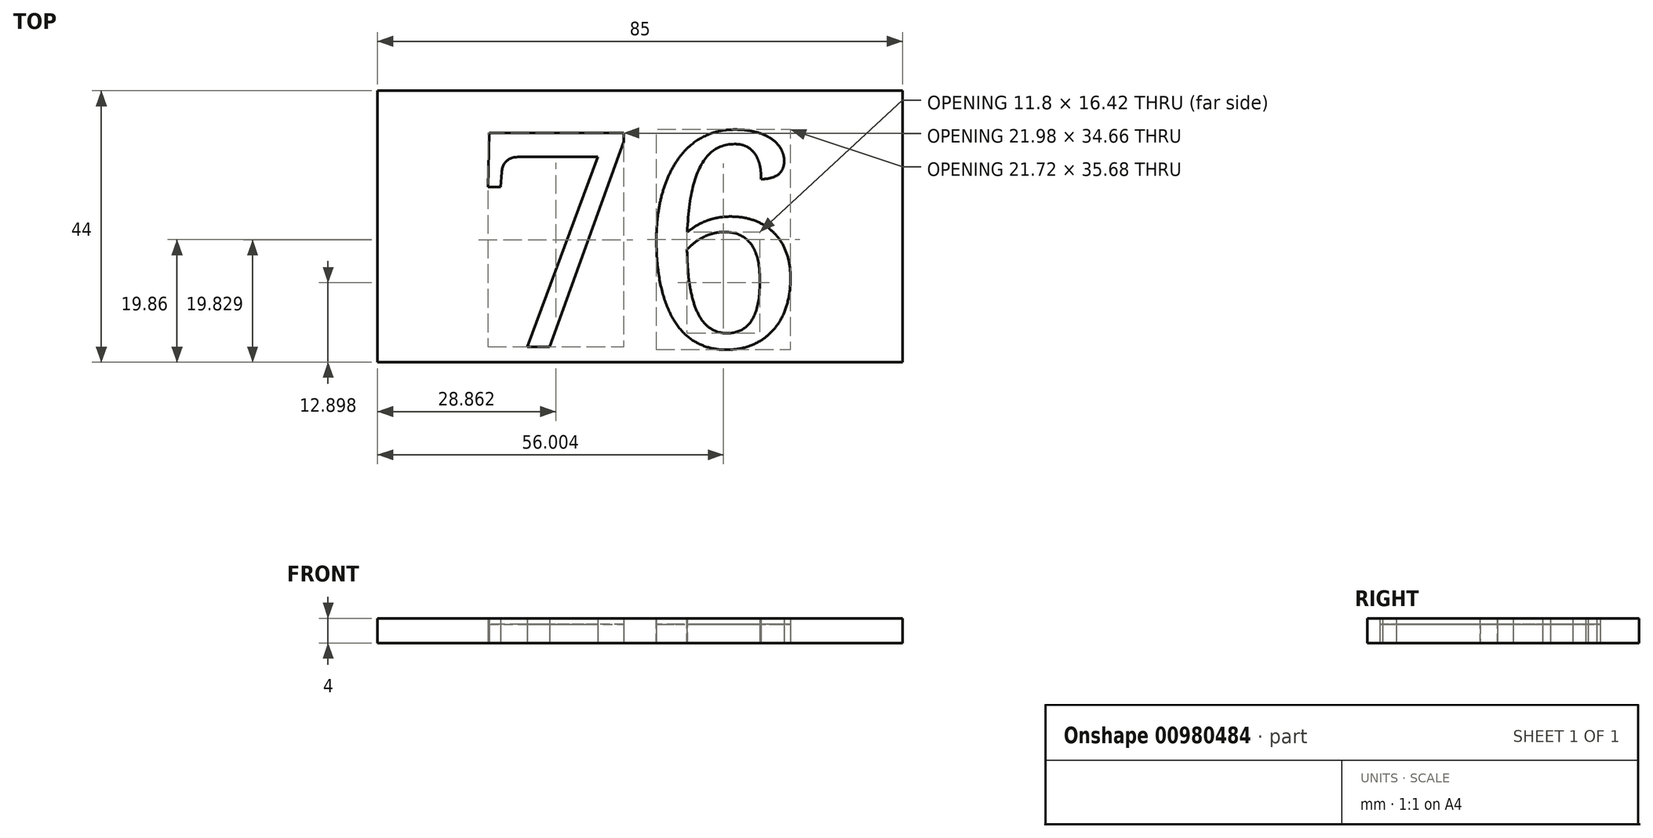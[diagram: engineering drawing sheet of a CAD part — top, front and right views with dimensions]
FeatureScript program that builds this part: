
annotation { "Feature Type Name" : "Feature", "Feature Type Description" : "" }
export const myFeature = defineFeature(function(context is Context, id is Id, definition is map)
    precondition{}
    {
        {
            var Q0;
            Q0=qCreatedBy(makeId("Top.planeOp"),FACE);
            var sketch = newSketch(context, id + "F0", { "sketchPlane" : qUnion([Q0])});
            skLineSegment(sketch, "E0.bottom", {"start": v(-42.5, 22) * mm, "end": v(42.5, 22) * mm});
            skLineSegment(sketch, "E0.top", {"start": v(-42.5, -22) * mm, "end": v(42.5, -22) * mm});
            skLineSegment(sketch, "E0.left", {"start": v(-42.5, 22) * mm, "end": v(-42.5, -22) * mm});
            skLineSegment(sketch, "E0.right", {"start": v(42.5, 22) * mm, "end": v(42.5, -22) * mm});
            skPoint(sketch, "E0.middle", {"position": v(0, 0) * mm});
            skText(sketch, "E1", { "text": "76\n", "fontName": "NotoSerif-Regular.ttf"});
            const initialGuessF0  = {"E1": [-0.0275, -0.0195, 1, 0, 0.035]};
            skSetInitialGuess(sketch, initialGuessF0);
            skSolve(sketch);
        }
        {
            var Q0;
            Q0=makeQuery(id+"F0.imprint","IMPRINT",FACE,{"disambiguationData":[TD([[makeQuery(id+"F0.imprint","IMPRINT",EDGE,{"derivedFrom":sQuery(id+"F0.wireOp",EDGE,"E0.bottom")}),-1.0]])]});
            var Q1;
            Q1=makeQuery(id+"F0.imprint","IMPRINT",FACE,{"disambiguationData":[TD([[makeQuery(id+"F0.imprint","IMPRINT",EDGE,{"derivedFrom":sQuery(id+"F0.wireOp",EDGE,"E1.sketch_text.stroke-44")}),1.0]])]});
            extrude(context, id + "F1", {"entities" : qUnion([Q0, Q1]), "depth" : 4 * mm, "offsetDistance" : 25 * mm});
        }
        {
            var Q0;
            Q0=makeQuery(id+"F0.imprint","IMPRINT",FACE,{"disambiguationData":[TD([[makeQuery(id+"F0.imprint","IMPRINT",EDGE,{"derivedFrom":sQuery(id+"F0.wireOp",EDGE,"E1.sketch_text.stroke-10")}),-1.0]])]});
            var Q1;
            Q1=makeQuery(id+"F0.imprint","IMPRINT",FACE,{"disambiguationData":[TD([[makeQuery(id+"F0.imprint","IMPRINT",EDGE,{"derivedFrom":sQuery(id+"F0.wireOp",EDGE,"E1.sketch_text.stroke-0")}),-1.0]])]});
            extrude(context, id + "F2", {"entities" : qUnion([Q0, Q1]), "depth" : 3 * mm, "offsetDistance" : 25 * mm});
        }
    });
